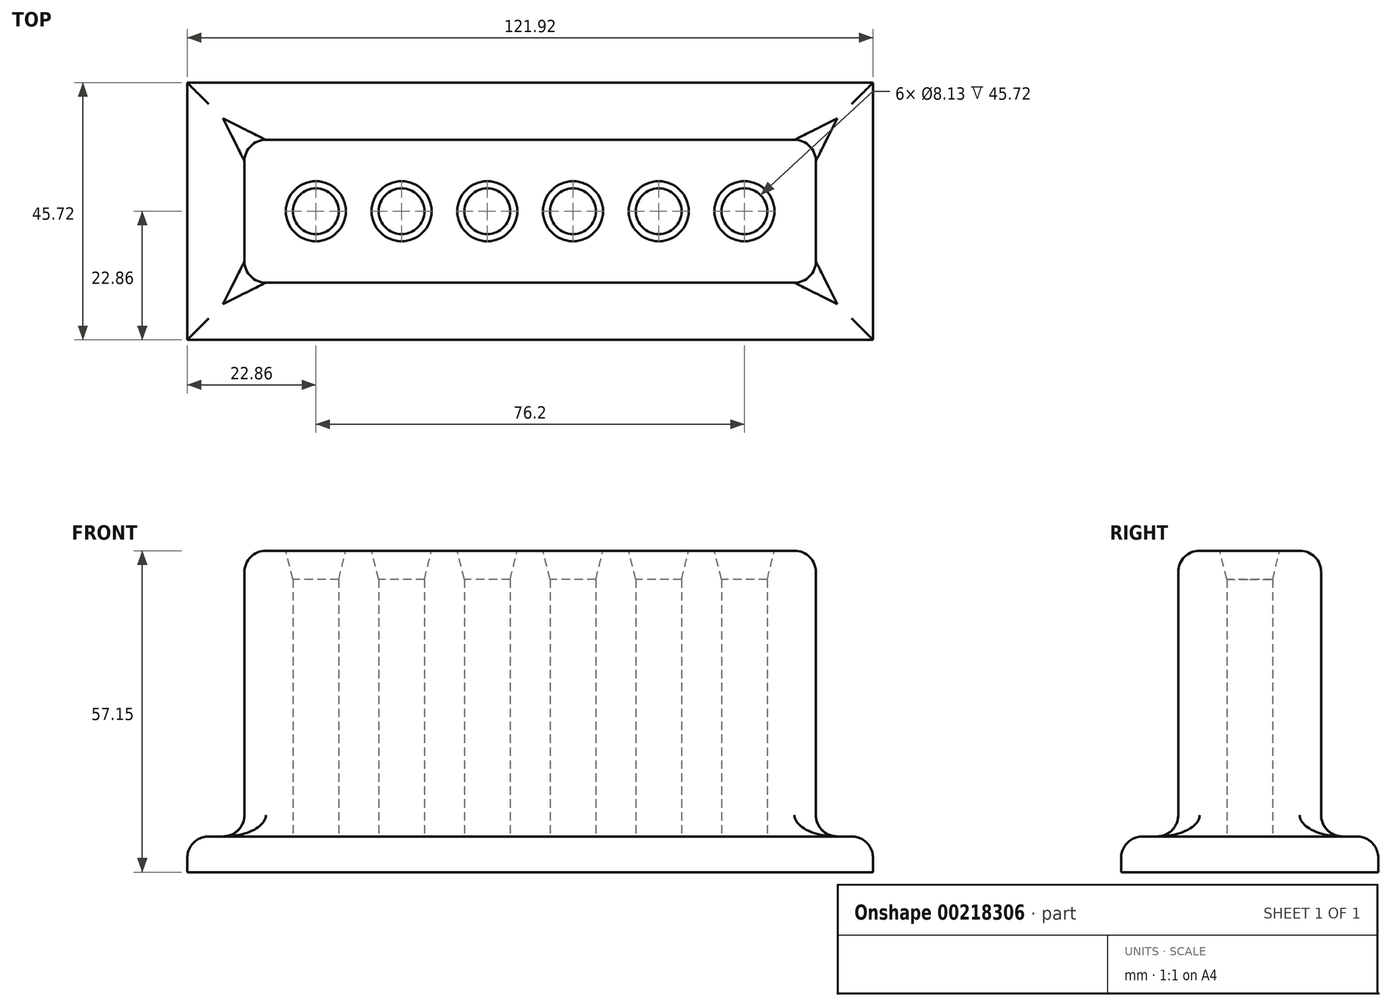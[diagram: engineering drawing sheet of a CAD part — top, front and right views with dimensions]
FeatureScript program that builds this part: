
annotation { "Feature Type Name" : "Feature", "Feature Type Description" : "" }
export const myFeature = defineFeature(function(context is Context, id is Id, definition is map)
    precondition{}
    {
        {
            var Q0;
            Q0=qCreatedBy(makeId("Top.planeOp"),FACE);
            var sketch = newSketch(context, id + "F0", { "sketchPlane" : qUnion([Q0])});
            skLineSegment(sketch, "E0.bottom", {"start": v(50.8, 12.7) * mm, "end": v(-50.8, 12.7) * mm});
            skLineSegment(sketch, "E0.top", {"start": v(50.8, -12.7) * mm, "end": v(-50.8, -12.7) * mm});
            skLineSegment(sketch, "E0.left", {"start": v(50.8, 12.7) * mm, "end": v(50.8, -12.7) * mm});
            skLineSegment(sketch, "E0.right", {"start": v(-50.8, 12.7) * mm, "end": v(-50.8, -12.7) * mm});
            skPoint(sketch, "E0.middle", {"position": v(0, 0) * mm});
            skCircle(sketch, "E1", {"center": v(-38.1, 0) * mm, "radius": 4.06 * mm});
            skCircle(sketch, "E2.1.0.0", {"center": v(-22.86, 0) * mm, "radius": 4.06 * mm});
            skCircle(sketch, "E2.2.0.0", {"center": v(-7.62, 0) * mm, "radius": 4.06 * mm});
            skCircle(sketch, "E2.3.0.0", {"center": v(7.62, 0) * mm, "radius": 4.06 * mm});
            skCircle(sketch, "E2.4.0.0", {"center": v(22.86, 0) * mm, "radius": 4.06 * mm});
            skCircle(sketch, "E2.5.0.0", {"center": v(38.1, 0) * mm, "radius": 4.06 * mm});
            skLineSegment(sketch, "E2.direction1", {"start": v(-38.1, 0) * mm, "end": v(-22.86, 0) * mm, "construction": true});
            skSolve(sketch);
        }
        {
            var Q0;
            Q0=qSketchRegion(id+"F0",true);
            extrude(context, id + "F1", {"entities" : qUnion([Q0]), "depth" : 50.8 * mm});
        }
        {
            var Q0;
            Q0=makeQuery(id+"F0.imprint","IMPRINT",FACE,{"disambiguationData":[TD([[makeQuery(id+"F0.imprint","IMPRINT",EDGE,{"derivedFrom":sQuery(id+"F0.wireOp",EDGE,"E0.bottom")}),1.0]])]});
            var sketch = newSketch(context, id + "F2", { "sketchPlane" : qUnion([Q0])});
            skLineSegment(sketch, "E3.bottom", {"start": v(60.96, -22.86) * mm, "end": v(-60.96, -22.86) * mm});
            skLineSegment(sketch, "E3.top", {"start": v(60.96, 22.86) * mm, "end": v(-60.96, 22.86) * mm});
            skLineSegment(sketch, "E3.left", {"start": v(60.96, -22.86) * mm, "end": v(60.96, 22.86) * mm});
            skLineSegment(sketch, "E3.right", {"start": v(-60.96, -22.86) * mm, "end": v(-60.96, 22.86) * mm});
            skPoint(sketch, "E3.middle", {"position": v(0, 0) * mm});
            skSolve(sketch);
        }
        {
            var Q0;
            Q0=qSketchRegion(id+"F2",true);
            extrude(context, id + "F3", {"entities" : qUnion([Q0]), "operationType" : NewBodyOperationType.ADD, "oppositeDirection" : true, "depth" : 6.35 * mm});
        }
        {
            var Q0;
            {var subQ0=sQuery(id+"F2.wireOp",EDGE,"E3.bottom");var subQ1=sQuery(id+"F2.wireOp",EDGE,"E3.top");var subQ2=sQuery(id+"F2.wireOp",EDGE,"E3.left");var subQ3=sQuery(id+"F2.wireOp",EDGE,"E3.right");Q0=makeQuery(id+"F3.boolean.opBoolean","SPLIT",FACE,{"disambiguationData":[TD([makeQuery(id+"F1.opExtrude","SWEPT_FACE",FACE,{"disambiguationData":[OSD([sQuery(id+"F0.wireOp",EDGE,"E0.bottom")])]})])],"derivedFrom":makeQuery(id+"F3.opExtrude","CAP_FACE",FACE,{"disambiguationData":[OSD([subQ0,subQ1,subQ2,subQ3])],"isStart":true})});}
            fillet(context, id + "F4", {"entities" : qUnion([Q0]), "radius" : 3.8 * mm, "tangentPropagation" : true, "allowEdgeOverflow" : false});
        }
        {
            var Q0;
            Q0=makeQuery(id+"F1.opExtrude","SWEPT_EDGE",EDGE,{"disambiguationData":[OSD([sQuery(id+"F0.wireOp",EDGE,"E0.bottom"),sQuery(id+"F0.wireOp",EDGE,"E0.right")])]});
            var Q1;
            Q1=makeQuery(id+"F1.opExtrude","SWEPT_EDGE",EDGE,{"disambiguationData":[OSD([sQuery(id+"F0.wireOp",EDGE,"E0.top"),sQuery(id+"F0.wireOp",EDGE,"E0.right")])]});
            var Q2;
            Q2=makeQuery(id+"F1.opExtrude","SWEPT_EDGE",EDGE,{"disambiguationData":[OSD([sQuery(id+"F0.wireOp",EDGE,"E0.top"),sQuery(id+"F0.wireOp",EDGE,"E0.left")])]});
            var Q3;
            Q3=makeQuery(id+"F1.opExtrude","SWEPT_EDGE",EDGE,{"disambiguationData":[OSD([sQuery(id+"F0.wireOp",EDGE,"E0.bottom"),sQuery(id+"F0.wireOp",EDGE,"E0.left")])]});
            var Q4;
            Q4=makeQuery(id+"F1.opExtrude","CAP_EDGE",EDGE,{"disambiguationData":[OSD([sQuery(id+"F0.wireOp",EDGE,"E0.left")])],"isStart":false});
            var Q5;
            Q5=makeQuery(id+"F1.opExtrude","CAP_EDGE",EDGE,{"disambiguationData":[OSD([sQuery(id+"F0.wireOp",EDGE,"E0.bottom")])],"isStart":false});
            var Q6;
            Q6=makeQuery(id+"F1.opExtrude","CAP_EDGE",EDGE,{"disambiguationData":[OSD([sQuery(id+"F0.wireOp",EDGE,"E0.right")])],"isStart":false});
            var Q7;
            Q7=makeQuery(id+"F1.opExtrude","CAP_EDGE",EDGE,{"disambiguationData":[OSD([sQuery(id+"F0.wireOp",EDGE,"E0.top")])],"isStart":false});
            fillet(context, id + "F5", {"entities" : qUnion([Q0, Q1, Q2, Q3, Q4, Q5, Q6, Q7]), "radius" : 3.8 * mm, "tangentPropagation" : true, "allowEdgeOverflow" : false});
        }
        {
            var Q0;
            Q0=makeQuery(id+"F1.opExtrude","CAP_EDGE",EDGE,{"disambiguationData":[OSD([sQuery(id+"F0.wireOp",EDGE,"E2.5.0.0")])],"isStart":false});
            var Q1;
            Q1=makeQuery(id+"F1.opExtrude","CAP_EDGE",EDGE,{"disambiguationData":[OSD([sQuery(id+"F0.wireOp",EDGE,"E2.4.0.0")])],"isStart":false});
            var Q2;
            Q2=makeQuery(id+"F1.opExtrude","CAP_EDGE",EDGE,{"disambiguationData":[OSD([sQuery(id+"F0.wireOp",EDGE,"E2.3.0.0")])],"isStart":false});
            var Q3;
            Q3=makeQuery(id+"F1.opExtrude","CAP_EDGE",EDGE,{"disambiguationData":[OSD([sQuery(id+"F0.wireOp",EDGE,"E2.2.0.0")])],"isStart":false});
            var Q4;
            Q4=makeQuery(id+"F1.opExtrude","CAP_EDGE",EDGE,{"disambiguationData":[OSD([sQuery(id+"F0.wireOp",EDGE,"E2.1.0.0")])],"isStart":false});
            var Q5;
            Q5=makeQuery(id+"F1.opExtrude","CAP_EDGE",EDGE,{"disambiguationData":[OSD([sQuery(id+"F0.wireOp",EDGE,"E1")])],"isStart":false});
            chamfer(context, id + "F6", {"entities" : qUnion([Q0, Q1, Q2, Q3, Q4, Q5]), "chamferType" : ChamferType.TWO_OFFSETS, "width1" : 5.08 * mm, "oppositeDirection" : false, "width2" : 1.27 * mm, "tangentPropagation" : true});
        }
    });
